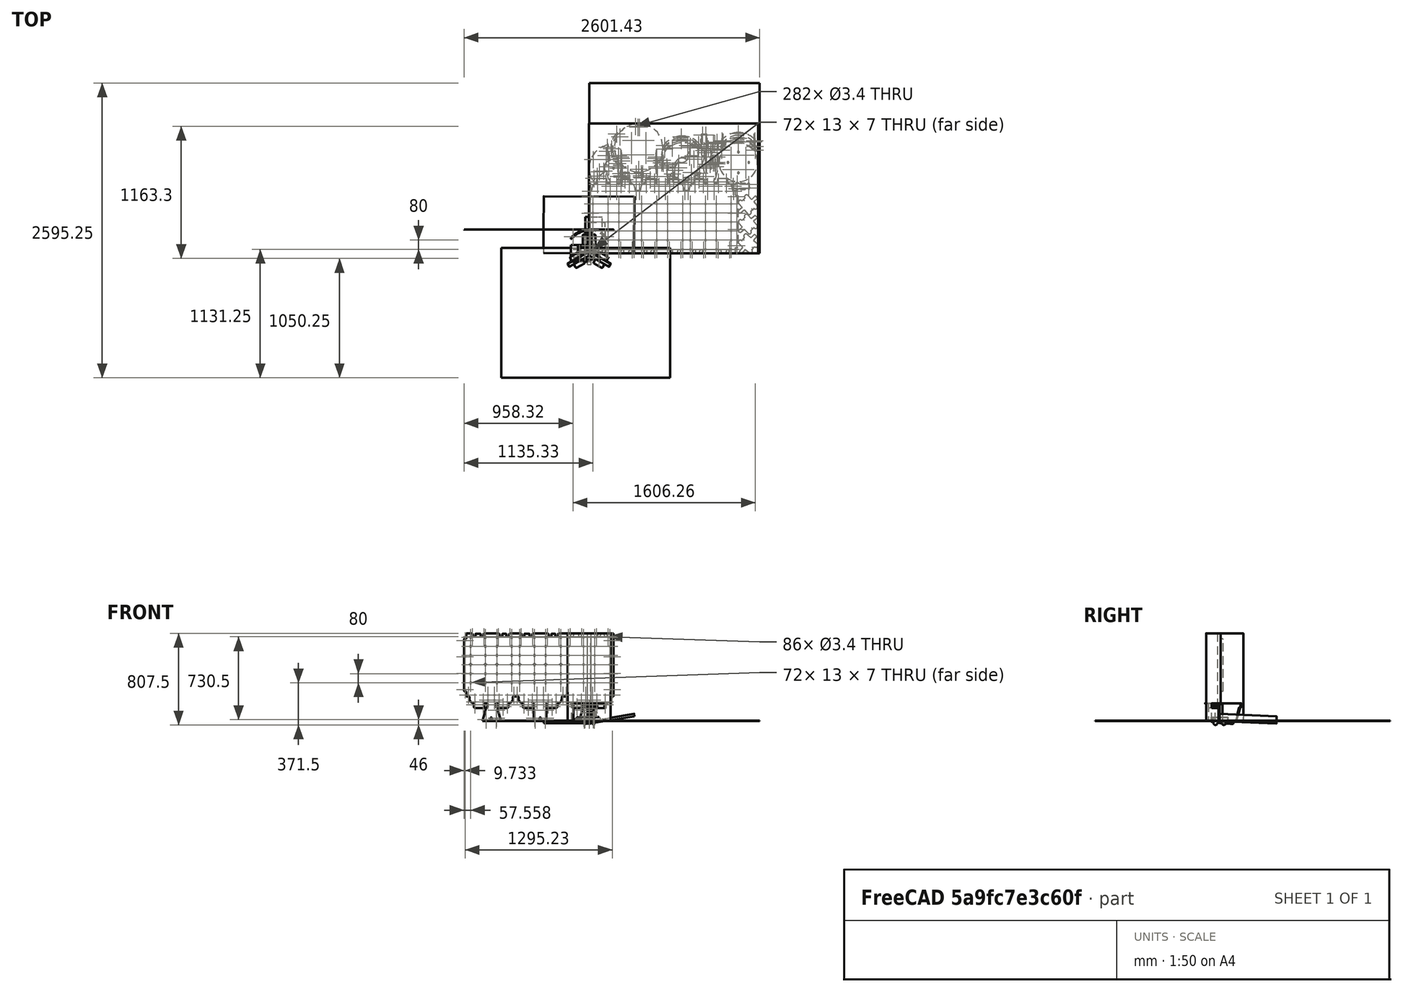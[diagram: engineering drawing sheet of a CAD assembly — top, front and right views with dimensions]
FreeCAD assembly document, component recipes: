
FREECAD ASSEMBLY — COMPONENT RECIPES ("composit_stand_small_3_vertDroppers")

This assembly document has 19 components, labeled P0..P18 below (a component is one placed body or linked part). 18 of them carry a construction recipe — the FreeCAD feature program that regenerates the part from scratch, quoted from this document or its linked companion documents; the rest are supplied as boundary geometry only. No exploded tour is included for this assembly.
NOTE — document 2 of 2 of this assembly tour. The two overview renders and the header above are repeated from document 1; the component sections below continue where the previous document stopped.
COMPONENT P17 — recipe-attached ("ugol_mini_material_0.30ansi", modeled in this document).
Construction recipe (the document's own serialized feature program — sketch geometry with constraints, then the solid features built on it; lengths are millimeters unless a unit is written):

FEATURE [PartDesign::CoordinateSystem] LCS_0005
  AttacherType = Attacher::AttachEngine3D
  MapMode = 2
  Support = -> [X_Axis035]
FEATURE [Sketcher::SketchObject] Sketch104
  FullyConstrained = false
  MapMode = 5
  Placement = pos=(0,0,0) rot=(0.57735,0.57735,0.57735;2.0944rad)
  Support = -> [YZ_Plane035]
  expr: Constraints[6] = 2mm + 0.5mm + 3.4mm + 2mm + 3mm
  sketch-geometry (3):
    g0: LineSegment StartX=10.9 StartY=0 StartZ=0 EndX=0 EndY=0 EndZ=0
    g1: LineSegment StartX=0 StartY=0 StartZ=0 EndX=0 EndY=17.2 EndZ=0
    g2: GeomPoint X=12.5 Y=0 Z=0
  constraints (7):
    c: PointOnObject(g0,g-1)
    c: Coincident(g0,g-1)
    c: Coincident(g0,g1)
    c: PointOnObject(g1,g-2)
    c: PointOnObject(g2,g-1)
    c: DistanceY(g1) = 17.2
    c: DistanceX(g0,g0) = 10.9
FEATURE [PartDesign::FeaturePython] BaseBend006  # WARN: FeaturePython — macro-defined, semantics opaque (R4)
  BendSide = 0
  BendSketch = -> Sketch104
  MidPlane = true
  Reverse = false
  length = 9.4
  radius = 2
  thickness = 0.5
  expr: length = <<main>>.rivet_d + 6mm
FEATURE [Sketcher::SketchObject] Sketch105
  AttachmentOffset = pos=(0,5.9,0) rot=(0,0,1;0rad)
  FullyConstrained = true
  MapMode = 5
  Placement = pos=(0,5.9,0) rot=(0,0,1;0rad)
  Support = -> [XY_Plane036]
  expr: .AttachmentOffset.Base.y = 2mm + 0.5mm + 2mm + 1.4mm
  expr: Constraints[1] = <<main>>.rivet_d
  sketch-geometry (1):
    g0: Circle CenterX=0 CenterY=0 CenterZ=0 NormalX=0 NormalY=0 NormalZ=1 AngleXU=0 Radius=1.7
  constraints (2):
    c: Coincident(g0,g-1)
    c: Diameter(g0) = 3.4
FEATURE [PartDesign::Plane] DatumPlane024
  AttachmentOffset = pos=(0,0,0) rot=(1,0,0;0.785398rad)
  Length = 61.8921
  MapMode = 5
  Placement = pos=(0,0,0) rot=(1,0,0;0.785398rad)
  ResizeMode = 0
  Support = -> [XY_Plane036]
  Width = 82.6027
FEATURE [PartDesign::Fillet] Fillet002
  Base = -> BaseBend006 [Edge25,Edge8]
  BaseFeature = -> BaseBend006
  Radius = 2
  SupportTransform = false
  UseAllEdges = false
FEATURE [PartDesign::Mirrored] Mirrored038
  BaseFeature = -> Fillet002
  MirrorPlane = -> YZ_Plane035
  Originals = -> [Fillet002]
FEATURE [PartDesign::Pocket] Pocket061
  BaseFeature = -> Mirrored038
  Direction = (0,0,-1)
  Length = 5
  Length2 = 5
  Midplane = true
  Profile = -> Sketch105
  ReferenceAxis = -> Sketch105 [N_Axis]
  Type = 1
FEATURE [Sketcher::SketchObject] Sketch106
  AttachmentOffset = pos=(0,12.5,0) rot=(0,0,1;0rad)
  FullyConstrained = true
  MapMode = 5
  Placement = pos=(0,-2.8e-15,12.5) rot=(1,0,0;1.5708rad)
  Support = -> [XZ_Plane035]
  expr: .AttachmentOffset.Base.y = 12.5mm
  expr: Constraints[1] = <<main>>.rivet_d
  sketch-geometry (1):
    g0: Circle CenterX=0 CenterY=0 CenterZ=0 NormalX=0 NormalY=0 NormalZ=1 AngleXU=0 Radius=1.7
  constraints (2):
    c: Coincident(g0,g-1)
    c: Diameter(g0) = 3.4
FEATURE [PartDesign::Pocket] Pocket062
  BaseFeature = -> Pocket061
  Direction = (0,1,2e-16)
  Length = 5
  Length2 = 5
  Midplane = true
  Profile = -> Sketch106
  ReferenceAxis = -> Sketch106 [N_Axis]
  Type = 1
FEATURE [PartDesign::Body] Body_7  label="ugol_mini_material_0.30ansi"
  Group = -> [LCS_0005,Sketch104,BaseBend006,Sketch105,DatumPlane024,Fillet002,Mirrored038,Pocket061,Sketch106,Pocket062]
  Origin = -> Origin035
  Tip = -> Pocket062
COMPONENT P18 — recipe-attached ("cover_bended_material_0.30ansi", modeled in this document).
Construction recipe (the document's own serialized feature program — sketch geometry with constraints, then the solid features built on it; lengths are millimeters unless a unit is written):

FEATURE [PartDesign::CoordinateSystem] LCS_0008
  AttacherType = Attacher::AttachEngine3D
  MapMode = 2
  Support = -> [X_Axis044]
FEATURE [Sketcher::SketchObject] Sketch138
  FullyConstrained = true
  MapMode = 5
  Support = -> [XY_Plane045]
  expr: Constraints[16] = Sketch003.Constraints.max_r
  expr: Constraints[17] = <<main>>.end_face_width / 2
  sketch-geometry (6):
    g0: LineSegment StartX=0 StartY=0 StartZ=0 EndX=181.736 EndY=104.925 EndZ=0
    g1: LineSegment StartX=0 StartY=39.9875 StartZ=0 EndX=1 EndY=39.9875 EndZ=0
    g2: LineSegment StartX=0 StartY=209.848 StartZ=0 EndX=1 EndY=209.848 EndZ=0
    g3: ArcOfCircle CenterX=0 CenterY=0 CenterZ=0 NormalX=0 NormalY=0 NormalZ=1 AngleXU=0 Radius=40 StartAngle=0.935116 EndAngle=1.54579
    g4: ArcOfCircle CenterX=0 CenterY=0 CenterZ=0 NormalX=0 NormalY=0 NormalZ=1 AngleXU=0 Radius=209.851 StartAngle=0.599917 EndAngle=1.56603
    g5: LineSegment StartX=23.749 StartY=32.1867 StartZ=0 EndX=173.207 EndY=118.476 EndZ=0
  constraints (19):
    c: Coincident(g0,g-1)
    c: Angle(g-1,g0) = 0.523599
    c: PointOnObject(g1,g-2)
    c: Horizontal(g1)
    c: PointOnObject(g2,g-2)
    c: Horizontal(g2)
    c: Vertical(g2,g1)
    c: DistanceX(g1) = 1
    c: Coincident(g3,g0)
    c: Coincident(g3,g1)
    c: Coincident(g4,g3)
    c: Coincident(g4,g2)
    c: Coincident(g5,g3)
    c: Coincident(g5,g4)
    c: Parallel(g5,g0)
    c: PointOnObject(g0,g4)
    c: DistanceY(g2) = 209.848
    c: Distance(g4,g0) = 16
    c: Diameter(g3) = 80
FEATURE [PartDesign::CoordinateSystem] Local_CS047
  AttacherType = Attacher::AttachEngine3D
  AttachmentOffset = pos=(0,0,0) rot=(-1,0,0;0.087266rad)
  MapMode = 5
  Placement = pos=(0,0,0) rot=(-1,0,0;0.087266rad)
  Support = -> [XY_Plane045]
FEATURE [PartDesign::CoordinateSystem] Local_CS048
  AttacherType = Attacher::AttachEngine3D
  AttachmentOffset = pos=(0,0,0) rot=(0.043053,-0.160675,0.986068;0.530656rad)
  MapMode = 5
  Placement = pos=(0,0,0) rot=(0.043053,-0.160675,0.986068;0.530656rad)
  Support = -> [XY_Plane045]
FEATURE [PartDesign::Line] DatumLine
  AttacherType = Attacher::AttachEngineLine
  Length = 20
  MapMode = 16
  Placement = pos=(0,0,0) rot=(0.363387,0.629406,0.686876;2.3865rad)
  ResizeMode = 0
  Support = -> [Local_CS048]
FEATURE [PartDesign::CoordinateSystem] Local_CS049
  AttacherType = Attacher::AttachEngine3D
  AttachmentOffset = pos=(0,0,0) rot=(0,0,-1;0.523599rad)
  MapMode = 5
  Placement = pos=(0,0,0) rot=(0.5,-0.866025,0;0.087266rad)
  Support = -> [Local_CS048]
FEATURE [Sketcher::SketchObject] Sketch139
  AttachmentOffset = pos=(0,0,0) rot=(1,0,0;1.48353rad)
  FullyConstrained = true
  MapMode = 5
  Placement = pos=(0,0,0) rot=(0.998509,-0.040244,0.036877;1.52867rad)
  Support = -> [Local_CS049]
  expr: Constraints[3] = 5
  sketch-geometry (2):
    g0: LineSegment StartX=0 StartY=0 StartZ=0 EndX=400 EndY=34.9955 EndZ=0
    g1: LineSegment StartX=0 StartY=0 StartZ=0 EndX=-400 EndY=34.9955 EndZ=0
  constraints (5):
    c: Coincident(g0,g-1)
    c: Coincident(g1,g0)
    c: Symmetric(g0,g1,g-2)
    c: Angle(g-1,g0) = 0.0872665
    c: DistanceX(g0) = 400
FEATURE [PartDesign::FeaturePython] BaseBend010  # WARN: FeaturePython — macro-defined, semantics opaque (R4)
  BendSide = 0
  BendSketch = -> Sketch139
  MidPlane = false
  Reverse = true
  length = 500
  radius = 0.1
  thickness = 0.3
FEATURE [Sketcher::SketchObject] Sketch140
  AttachmentOffset = pos=(0,0,0) rot=(0,1,0;-0.087266rad)
  ExternalGeometry = -> [Sketch138]
  FullyConstrained = false
  MapMode = 5
  Placement = pos=(0,0,0) rot=(-0.258803,0.965864,0.0113;6.1146rad)
  Support = -> [Local_CS049]
  sketch-geometry (14):
    g0: LineSegment StartX=23.2598 StartY=32.117 StartZ=0 EndX=170.272 EndY=118.078 EndZ=0
    g1: ArcOfEllipse CenterX=1 CenterY=7.19572 CenterZ=0 NormalX=0 NormalY=0 NormalZ=1 MajorRadius=202.441 MinorRadius=202.319 AngleXU=-1.5708 StartAngle=2.15044 EndAngle=3.14159
    g2: LineSegment StartX=1 StartY=-195.245 StartZ=0 EndX=1 EndY=209.636 EndZ=0
    g3: LineSegment StartX=203.319 StartY=7.19572 StartZ=0 EndX=-201.319 EndY=7.19572 EndZ=0
    g4: GeomPoint X=1 Y=0.187598 Z=0
    g5: GeomPoint X=1 Y=14.2038 Z=0
    g6: LineSegment StartX=0 StartY=209.636 StartZ=0 EndX=1 EndY=209.636 EndZ=0
    g7: LineSegment StartX=0 StartY=39.0768 StartZ=0 EndX=1 EndY=39.0768 EndZ=0
    g8: ArcOfCircle CenterX=1 CenterY=0 CenterZ=0 NormalX=0 NormalY=0 NormalZ=1 AngleXU=0 Radius=39.0768 StartAngle=0.964726 EndAngle=1.5708
    g9: LineSegment StartX=0 StartY=-278.705 StartZ=0 EndX=616.451 EndY=-278.705 EndZ=0
    g10: LineSegment StartX=616.451 StartY=-278.705 StartZ=0 EndX=616.451 EndY=663.316 EndZ=0
    g11: LineSegment StartX=616.451 StartY=663.316 StartZ=0 EndX=0 EndY=663.316 EndZ=0
    g12: LineSegment StartX=0 StartY=663.316 StartZ=0 EndX=0 EndY=209.636 EndZ=0
    g13: LineSegment StartX=0 StartY=39.0768 StartZ=0 EndX=0 EndY=-278.705 EndZ=0
  constraints (27):
    c: Coincident(g0,g-3)
    c: Coincident(g0,g-3)
    c: InternalAlignment(g2-g5 -> g1) x4
    c: Horizontal(g3)
    c: Coincident(g1,g0)
    c: PointOnObject(g6,g-2)
    c: Horizontal(g6)
    c: Tangent(g1,g6) = 1.5708
    c: PointOnObject(g7,g-2)
    c: Horizontal(g7)
    c: Coincident(g8,g0)
    c: Tangent(g7,g8) = 1.5708
    c: Vertical(g7,g1)
    c: DistanceX(g1) = 1
    c: PointOnObject(g1,g-4)
    c: Horizontal(g8,g-4)
    c: Coincident(g9,g10)
    c: Coincident(g10,g11)
    c: Coincident(g11,g12)
    c: Coincident(g13,g9)
    c: Horizontal(g9)
    c: Horizontal(g11)
    c: Vertical(g10)
    c: Vertical(g12)
    c: PointOnObject(g9,g-2)
    c: Coincident(g13,g7)
    c: Coincident(g12,g6)
FEATURE [Sketcher::SketchObject] Sketch141
  AttachmentOffset = pos=(0,0,0) rot=(1,0,0;-0.087266rad)
  ExternalGeometry = -> [Sketch140]
  FullyConstrained = false
  MapMode = 5
  Placement = pos=(0,0,0) rot=(1,0,0;6.19592rad)
  Support = -> [XY_Plane045]
  sketch-geometry (10):
    g0: LineSegment StartX=-0.5 StartY=38.7427 StartZ=0 EndX=-0.5 EndY=0 EndZ=0
    g1: LineSegment StartX=-0.5 StartY=0 StartZ=0 EndX=0.5 EndY=0 EndZ=0
    g2: LineSegment StartX=0.5 StartY=0 StartZ=0 EndX=0.5 EndY=38.7427 EndZ=0
    g3: LineSegment StartX=0.5 StartY=38.7427 StartZ=0 EndX=-0.5 EndY=38.7427 EndZ=0
    g4: GeomPoint X=0 Y=19.3713 Z=0
    g5: LineSegment StartX=-0.5 StartY=207.844 StartZ=0 EndX=-0.5 EndY=768.027 EndZ=0
    g6: LineSegment StartX=-0.5 StartY=768.027 StartZ=0 EndX=0.5 EndY=768.027 EndZ=0
    g7: LineSegment StartX=0.5 StartY=768.027 StartZ=0 EndX=0.5 EndY=207.844 EndZ=0
    g8: LineSegment StartX=0.5 StartY=207.844 StartZ=0 EndX=-0.5 EndY=207.844 EndZ=0
    g9: GeomPoint X=0 Y=487.936 Z=0
  constraints (25):
    c: Coincident(g0,g1)
    c: Coincident(g1,g2)
    c: Coincident(g2,g3)
    c: Coincident(g3,g0)
    c: Horizontal(g1)
    c: Horizontal(g3)
    c: Vertical(g0)
    c: Vertical(g2)
    c: Symmetric(g1,g0,g4)
    c: PointOnObject(g4,g-2)
    c: PointOnObject(g1,g-1)
    c: Coincident(g5,g6)
    c: Coincident(g6,g7)
    c: Coincident(g7,g8)
    c: Coincident(g8,g5)
    c: Horizontal(g6)
    c: Horizontal(g8)
    c: Vertical(g5)
    c: Vertical(g7)
    c: Symmetric(g6,g5,g9)
    c: PointOnObject(g9,g-2)
    c: DistanceX(g6,g6) = 1
    c: DistanceX(g3,g3) = 1
    c: PointOnObject(g-4,g8)
    c: PointOnObject(g-3,g3)
FEATURE [PartDesign::Pocket] Pocket096
  BaseFeature = -> BaseBend010
  Direction = (0,-0.0871557,-0.996195)
  Length = 5
  Length2 = 5
  Midplane = true
  Profile = -> Sketch141
  ReferenceAxis = -> Sketch141 [N_Axis]
  Refine = true
  Type = 1
FEATURE [PartDesign::Pocket] Pocket095
  BaseFeature = -> Pocket096
  Direction = (0.162099,0.0432684,-0.985825)
  Length = 5
  Length2 = 5
  Midplane = true
  Profile = -> Sketch140
  ReferenceAxis = -> Sketch140 [N_Axis]
  Type = 1
FEATURE [PartDesign::Mirrored] Mirrored041
  BaseFeature = -> Pocket095
  MirrorPlane = -> YZ_Plane044
  Originals = -> [Pocket095]
  Refine = true
FEATURE [PartDesign::Body] cover_bender  label="cover_bended_material_0.30ansi"
  Group = -> [LCS_0008,Sketch138,Sketch139,BaseBend010,Local_CS047,Pocket096,Sketch140,Pocket095,Mirrored041,Sketch141,Local_CS048,DatumLine,Local_CS049]
  Origin = -> Origin044
  Tip = -> BaseBend010
PROVENANCE & LICENSES
A FreeCAD (.FCStd) document from a public repository crawl; recipes are the document's own serialized feature recipes (and, for linked parts, companion documents' recipes).
License: as declared in the source repository (recorded in the dataset sidecar).
